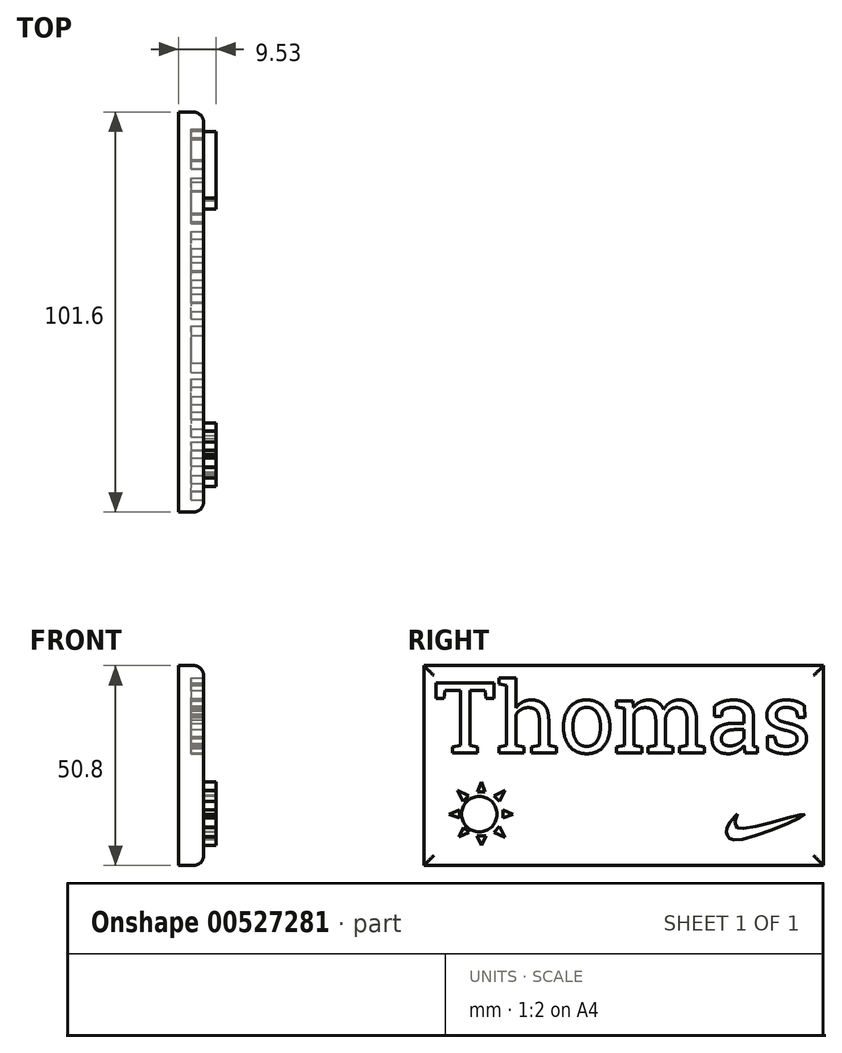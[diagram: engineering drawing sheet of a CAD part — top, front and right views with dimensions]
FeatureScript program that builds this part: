
annotation { "Feature Type Name" : "Feature", "Feature Type Description" : "" }
export const myFeature = defineFeature(function(context is Context, id is Id, definition is map)
    precondition{}
    {
        {
            var Q0;
            Q0=qCreatedBy(makeId("Right.planeOp"),FACE);
            var sketch = newSketch(context, id + "F0", { "sketchPlane" : qUnion([Q0])});
            skLineSegment(sketch, "E0.bottom", {"start": v(-48.96, 25.34) * mm, "end": v(52.64, 25.34) * mm});
            skLineSegment(sketch, "E0.top", {"start": v(-48.96, -25.46) * mm, "end": v(52.64, -25.46) * mm});
            skLineSegment(sketch, "E0.left", {"start": v(-48.96, 25.34) * mm, "end": v(-48.96, -25.46) * mm});
            skLineSegment(sketch, "E0.right", {"start": v(52.64, 25.34) * mm, "end": v(52.64, -25.46) * mm});
            skSolve(sketch);
        }
        {
            var Q0;
            Q0=makeQuery(id+"F0.imprint","IMPRINT",FACE,{"disambiguationData":[TD([[makeQuery(id+"F0.imprint","IMPRINT",EDGE,{"derivedFrom":sQuery(id+"F0.wireOp",EDGE,"E0.bottom")}),-1.0]])]});
            extrude(context, id + "F1", {"entities" : qUnion([Q0]), "oppositeDirection" : true, "depth" : 6.35 * mm, "offsetDistance" : 25.4 * mm});
        }
        {
            var Q0;
            Q0=makeQuery(id+"F0.imprint","IMPRINT",FACE,{"disambiguationData":[TD([[makeQuery(id+"F0.imprint","IMPRINT",EDGE,{"derivedFrom":sQuery(id+"F0.wireOp",EDGE,"E0.bottom")}),-1.0]])]});
            var sketch = newSketch(context, id + "F2", { "sketchPlane" : qUnion([Q0])});
            skText(sketch, "E1", { "text": "Thomas", "fontName": "RobotoSlab-Regular.ttf"});
            const initialGuessF2  = {"E1": [-0.0463, 0.00317, 1, 0, 0.01796]};
            skSetInitialGuess(sketch, initialGuessF2);
            skSolve(sketch);
        }
        {
            var Q0;
            Q0 = qSketchRegion(id + "F2", true);
            extrude(context, id + "F3", {"entities" : qUnion([Q0]), "operationType" : NewBodyOperationType.REMOVE, "oppositeDirection" : true, "depth" : 3.17 * mm, "offsetDistance" : 25.4 * mm});
        }
        {
            var Q0;
            Q0=makeQuery(id+"F0.imprint","IMPRINT",FACE,{"disambiguationData":[TD([[makeQuery(id+"F0.imprint","IMPRINT",EDGE,{"derivedFrom":sQuery(id+"F0.wireOp",EDGE,"E0.bottom")}),-1.0]])]});
            var sketch = newSketch(context, id + "F4", { "sketchPlane" : qUnion([Q0])});
            skCircle(sketch, "E2", {"center": v(-34.85, -12.43) * mm, "radius": 4.5 * mm});
            skLineSegment(sketch, "E3", {"start": v(-35.3, -6.76) * mm, "end": v(-33.4, -6.76) * mm});
            skLineSegment(sketch, "E4", {"start": v(-34.34, -4.25) * mm, "end": v(-33.4, -6.76) * mm});
            skLineSegment(sketch, "E5", {"start": v(-35.3, -6.76) * mm, "end": v(-34.34, -4.25) * mm});
            skLineSegment(sketch, "E6", {"start": v(-31.16, -7.79) * mm, "end": v(-29.68, -9.21) * mm});
            skLineSegment(sketch, "E7", {"start": v(-29.68, -9.21) * mm, "end": v(-28.35, -6.38) * mm});
            skLineSegment(sketch, "E8", {"start": v(-28.35, -6.38) * mm, "end": v(-31.16, -7.79) * mm});
            skLineSegment(sketch, "E9", {"start": v(-37.55, -7.8) * mm, "end": v(-38.96, -9.21) * mm});
            skPoint(sketch, "E9.startSnap0", {"position": v(-29.01, -7.8) * mm});
            skLineSegment(sketch, "E10", {"start": v(-38.96, -9.21) * mm, "end": v(-40.38, -6.38) * mm});
            skLineSegment(sketch, "E11", {"start": v(-40.38, -6.38) * mm, "end": v(-37.71, -7.63) * mm});
            skLineSegment(sketch, "E12", {"start": v(-37.71, -7.63) * mm, "end": v(-37.55, -7.8) * mm});
            skLineSegment(sketch, "E13", {"start": v(-39.87, -11.33) * mm, "end": v(-39.87, -13.36) * mm});
            skLineSegment(sketch, "E14", {"start": v(-39.87, -13.36) * mm, "end": v(-42.54, -12.43) * mm});
            skLineSegment(sketch, "E15", {"start": v(-42.54, -12.43) * mm, "end": v(-39.87, -11.33) * mm});
            skLineSegment(sketch, "E16", {"start": v(-28.8, -11.33) * mm, "end": v(-28.8, -13.36) * mm});
            skLineSegment(sketch, "E17", {"start": v(-28.8, -13.36) * mm, "end": v(-26.33, -12.43) * mm});
            skLineSegment(sketch, "E18", {"start": v(-26.33, -12.43) * mm, "end": v(-28.8, -11.33) * mm});
            skLineSegment(sketch, "E19", {"start": v(-38.92, -15.74) * mm, "end": v(-37.5, -17.07) * mm});
            skLineSegment(sketch, "E20", {"start": v(-37.5, -17.07) * mm, "end": v(-40.07, -18.21) * mm});
            skLineSegment(sketch, "E21", {"start": v(-40.07, -18.21) * mm, "end": v(-38.92, -15.74) * mm});
            skLineSegment(sketch, "E22", {"start": v(-29.7, -15.58) * mm, "end": v(-31.17, -17.07) * mm});
            skLineSegment(sketch, "E23", {"start": v(-31.17, -17.07) * mm, "end": v(-28.38, -18.4) * mm});
            skLineSegment(sketch, "E24", {"start": v(-28.38, -18.4) * mm, "end": v(-29.7, -15.58) * mm});
            skLineSegment(sketch, "E25", {"start": v(-35.45, -17.94) * mm, "end": v(-33.14, -17.94) * mm});
            skLineSegment(sketch, "E26", {"start": v(-33.14, -17.94) * mm, "end": v(-34.3, -20.4) * mm});
            skLineSegment(sketch, "E27", {"start": v(-34.3, -20.4) * mm, "end": v(-35.45, -17.94) * mm});
            skSolve(sketch);
        }
        {
            var Q0;
            Q0 = qSketchRegion(id + "F4", true);
            extrude(context, id + "F5", {"entities" : qUnion([Q0]), "operationType" : NewBodyOperationType.ADD, "depth" : 3.17 * mm, "offsetDistance" : 25.4 * mm});
        }
        {
            var Q0;
            Q0=makeQuery(id+"F2.imprint","IMPRINT",FACE,{"disambiguationData":[TD([[makeQuery(id+"F2.imprint","IMPRINT",EDGE,{"derivedFrom":sQuery(id+"F2.wireOp",EDGE,"E1.sketch_text.stroke-0")}),1.0]])]});
            var sketch = newSketch(context, id + "F6", { "sketchPlane" : qUnion([Q0])});
            skFitSpline(sketch, "E28", {"points": [v(30.78, -12.31) * mm, v(30.15, -13.97) * mm, v(30.39, -15.43) * mm, v(31.69, -16.14) * mm, v(47.7, -12.47) * mm, v(31.77, -18.86) * mm, v(28.45, -18.3) * mm, v(28.02, -17.24) * mm, v(28.41, -15.15) * mm, v(30.78, -12.31) * mm]});
            skSolve(sketch);
        }
        {
            var Q0;
            Q0 = qSketchRegion(id + "F6", true);
            extrude(context, id + "F7", {"entities" : qUnion([Q0]), "operationType" : NewBodyOperationType.ADD, "depth" : 3.17 * mm, "offsetDistance" : 25.4 * mm});
        }
        {
            var Q0;
            Q0=makeQuery(id+"F1.opExtrude","CAP_EDGE",EDGE,{"disambiguationData":[OSD([sQuery(id+"F0.wireOp",EDGE,"E0.left")])],"isStart":true});
            var Q1;
            Q1=makeQuery(id+"F1.opExtrude","CAP_EDGE",EDGE,{"disambiguationData":[OSD([sQuery(id+"F0.wireOp",EDGE,"E0.right")])],"isStart":true});
            var Q2;
            Q2=makeQuery(id+"F1.opExtrude","CAP_EDGE",EDGE,{"disambiguationData":[OSD([sQuery(id+"F0.wireOp",EDGE,"E0.bottom")])],"isStart":true});
            var Q3;
            Q3=makeQuery(id+"F1.opExtrude","CAP_EDGE",EDGE,{"disambiguationData":[OSD([sQuery(id+"F0.wireOp",EDGE,"E0.top")])],"isStart":true});
            fillet(context, id + "F8", {"entities" : qUnion([Q0, Q1, Q2, Q3]), "radius" : 2.54 * mm, "tangentPropagation" : true, "allowEdgeOverflow" : false});
        }
    });
